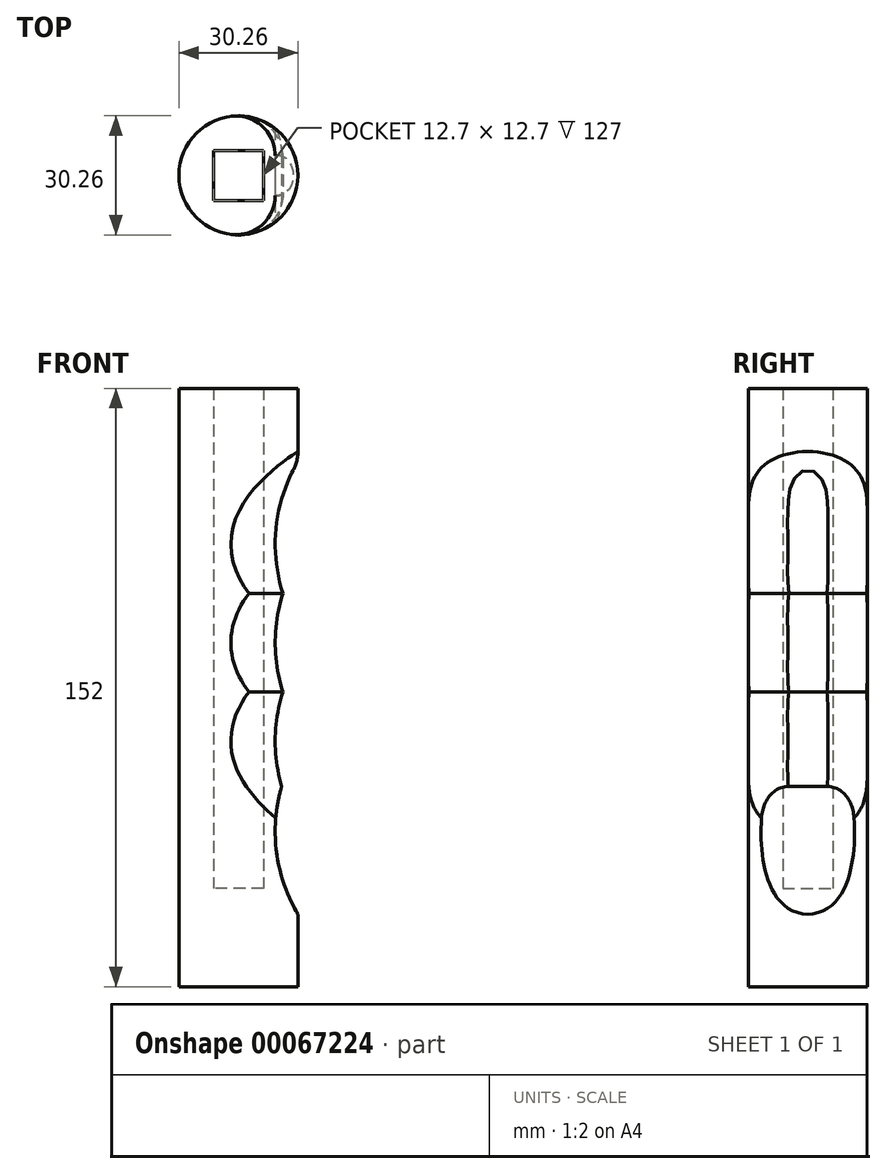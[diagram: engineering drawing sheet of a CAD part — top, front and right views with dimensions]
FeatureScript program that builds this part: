
annotation { "Feature Type Name" : "Feature", "Feature Type Description" : "" }
export const myFeature = defineFeature(function(context is Context, id is Id, definition is map)
    precondition{}
    {
        {
            var Q0;
            Q0=qCreatedBy(makeId("Top.planeOp"),FACE);
            var sketch = newSketch(context, id + "F0", { "sketchPlane" : qUnion([Q0])});
            skCircle(sketch, "E0", {"center": v(0, 0) * mm, "radius": 15.12 * mm});
            skLineSegment(sketch, "E1", {"start": v(-6.35, 0) * mm, "end": v(-6.35, -6.35) * mm});
            skLineSegment(sketch, "E2", {"start": v(-6.35, -6.35) * mm, "end": v(6.35, -6.35) * mm});
            skLineSegment(sketch, "E3", {"start": v(6.35, -6.35) * mm, "end": v(6.35, 6.35) * mm});
            skLineSegment(sketch, "E4", {"start": v(6.35, 6.35) * mm, "end": v(-6.35, 6.35) * mm});
            skLineSegment(sketch, "E5", {"start": v(-6.35, 0) * mm, "end": v(-6.35, 6.35) * mm});
            skSolve(sketch);
        }
        {
            var Q0;
            Q0=makeQuery(id+"F0.imprint","IMPRINT",FACE,{"disambiguationData":[TD([[makeQuery(id+"F0.imprint","IMPRINT",EDGE,{"derivedFrom":sQuery(id+"F0.wireOp",EDGE,"E0")}),1.0]])]});
            extrude(context, id + "F1", {"entities" : qUnion([Q0]), "depth" : 127 * mm});
        }
        {
            var Q0;
            Q0=makeQuery(id+"F1.opExtrude","CAP_FACE",FACE,{"disambiguationData":[OSD([sQuery(id+"F0.wireOp",EDGE,"E0"),sQuery(id+"F0.wireOp",EDGE,"268feebe-71f6-42c3-a029-8ffc5a6c32c5")])],"isStart":true});
            var sketch = newSketch(context, id + "F2", { "sketchPlane" : qUnion([Q0])});
            skCircle(sketch, "E6.0", {"center": v(0, 0) * mm, "radius": 15.12 * mm});
            skSolve(sketch);
        }
        {
            var Q0;
            Q0=makeQuery(id+"F2.imprint","IMPRINT",FACE,{"disambiguationData":[TD([[makeQuery(id+"F2.imprint","IMPRINT",EDGE,{"derivedFrom":sQuery(id+"F2.wireOp",EDGE,"E6.0")}),-1.0]])]});
            extrude(context, id + "F3", {"entities" : qUnion([Q0]), "operationType" : NewBodyOperationType.ADD, "depth" : 25 * mm});
        }
        {
            var Q0;
            Q0=qCreatedBy(makeId("Top.planeOp"),FACE);
            var sketch = newSketch(context, id + "F4", { "sketchPlane" : qUnion([Q0])});
            skLineSegment(sketch, "E7.0.1", {"start": v(-6.35, -6.35) * mm, "end": v(-6.35, 6.35) * mm});
            skLineSegment(sketch, "E7.0.3", {"start": v(-6.35, 6.35) * mm, "end": v(-6.35, -6.35) * mm});
            skLineSegment(sketch, "E8.0", {"start": v(-6.35, -6.35) * mm, "end": v(6.35, -6.35) * mm});
            skLineSegment(sketch, "E9.0", {"start": v(6.35, -6.35) * mm, "end": v(6.35, 6.35) * mm});
            skLineSegment(sketch, "E10.0", {"start": v(6.35, 6.35) * mm, "end": v(-6.35, 6.35) * mm});
            skSolve(sketch);
        }
        {
            var Q0;
            Q0=qCreatedBy(makeId("Front.planeOp"),FACE);
            var sketch = newSketch(context, id + "F5", { "sketchPlane" : qUnion([Q0])});
            skLineSegment(sketch, "E11", {"start": v(15.12, 127) * mm, "end": v(15.12, -25) * mm});
            skLineSegment(sketch, "E12", {"start": v(15.12, 127) * mm, "end": v(50.35, 127) * mm});
            skLineSegment(sketch, "E13", {"start": v(50.35, 127) * mm, "end": v(50.35, -25) * mm});
            skLineSegment(sketch, "E14", {"start": v(15.12, -25) * mm, "end": v(50.35, -25) * mm});
            skCircle(sketch, "E15", {"center": v(50.35, 14.4) * mm, "radius": 41 * mm});
            skCircle(sketch, "E16", {"center": v(50.35, 37.4) * mm, "radius": 41 * mm});
            skCircle(sketch, "E17", {"center": v(50.35, 62.4) * mm, "radius": 41 * mm});
            skCircle(sketch, "E18", {"center": v(50.35, 87.4) * mm, "radius": 41 * mm});
            skLineSegment(sketch, "E19", {"start": v(-6.88, 0) * mm, "end": v(-6.88, 127) * mm});
            skLineSegment(sketch, "E20", {"start": v(6.88, 127) * mm, "end": v(6.88, 0) * mm});
            skLineSegment(sketch, "E21", {"start": v(-15.12, -25) * mm, "end": v(-15.12, 127) * mm});
            skSolve(sketch);
        }
        {
            var Q0;
            Q0=qSketchRegion(id+"F5",true);
            extrude(context, id + "F6", {"entities" : qUnion([Q0]), "operationType" : NewBodyOperationType.REMOVE, "oppositeDirection" : true, "depth" : 50 * mm, "symmetric" : true});
        }
        {
            var Q0;
            {var subQ0=sQuery(id+"F5.wireOp",EDGE,"E18");Q0=makeQuery(id+"F6.boolean.opBoolean","INTERSECT",EDGE,{"derivedFrom":[makeQuery(id+"F3.boolean.opBoolean","MERGE",FACE,{"derivedFrom":[makeQuery(id+"F1.opExtrude","SWEPT_FACE",FACE,{"disambiguationData":[OSD([sQuery(id+"F0.wireOp",EDGE,"E0")])]}),makeQuery(id+"F3.opExtrude","SWEPT_FACE",FACE,{"disambiguationData":[OSD([sQuery(id+"F2.wireOp",EDGE,"E6.0")])]})]}),makeQuery(id+"F6.opExtrude","SWEPT_FACE",FACE,{"disambiguationData":[OSD([subQ0]),TDD([makeQuery(id+"F5.imprint","IMPRINT",EDGE,{"disambiguationData":[TD([[makeQuery(id+"F5.imprint","INTERSECT",VERTEX,{"disambiguationData":[OD(0.0)],"derivedFrom":[sQuery(id+"F5.wireOp",EDGE,"E11"),subQ0]}),-1.0]])],"derivedFrom":subQ0})])]})]});}
            var Q1;
            {var subQ0=sQuery(id+"F5.wireOp",EDGE,"E17");Q1=makeQuery(id+"F6.boolean.opBoolean","INTERSECT",EDGE,{"disambiguationData":[OD(0.0)],"derivedFrom":[makeQuery(id+"F3.boolean.opBoolean","MERGE",FACE,{"derivedFrom":[makeQuery(id+"F1.opExtrude","SWEPT_FACE",FACE,{"disambiguationData":[OSD([sQuery(id+"F0.wireOp",EDGE,"E0")])]}),makeQuery(id+"F3.opExtrude","SWEPT_FACE",FACE,{"disambiguationData":[OSD([sQuery(id+"F2.wireOp",EDGE,"E6.0")])]})]}),makeQuery(id+"F6.opExtrude","SWEPT_FACE",FACE,{"disambiguationData":[OSD([subQ0]),TDD([makeQuery(id+"F5.imprint","IMPRINT",EDGE,{"disambiguationData":[TD([[makeQuery(id+"F5.imprint","INTERSECT",VERTEX,{"disambiguationData":[OD(1.0)],"derivedFrom":[sQuery(id+"F5.wireOp",EDGE,"E16"),subQ0]}),1.0]])],"derivedFrom":subQ0})])]})]});}
            var Q2;
            {var subQ0=sQuery(id+"F5.wireOp",EDGE,"E17");Q2=makeQuery(id+"F6.boolean.opBoolean","INTERSECT",EDGE,{"disambiguationData":[OD(1.0)],"derivedFrom":[makeQuery(id+"F3.boolean.opBoolean","MERGE",FACE,{"derivedFrom":[makeQuery(id+"F1.opExtrude","SWEPT_FACE",FACE,{"disambiguationData":[OSD([sQuery(id+"F0.wireOp",EDGE,"E0")])]}),makeQuery(id+"F3.opExtrude","SWEPT_FACE",FACE,{"disambiguationData":[OSD([sQuery(id+"F2.wireOp",EDGE,"E6.0")])]})]}),makeQuery(id+"F6.opExtrude","SWEPT_FACE",FACE,{"disambiguationData":[OSD([subQ0]),TDD([makeQuery(id+"F5.imprint","IMPRINT",EDGE,{"disambiguationData":[TD([[makeQuery(id+"F5.imprint","INTERSECT",VERTEX,{"disambiguationData":[OD(1.0)],"derivedFrom":[sQuery(id+"F5.wireOp",EDGE,"E16"),subQ0]}),1.0]])],"derivedFrom":subQ0})])]})]});}
            var Q3;
            {var subQ0=sQuery(id+"F5.wireOp",EDGE,"E16");Q3=makeQuery(id+"F6.boolean.opBoolean","INTERSECT",EDGE,{"disambiguationData":[OD(1.0)],"derivedFrom":[makeQuery(id+"F3.boolean.opBoolean","MERGE",FACE,{"derivedFrom":[makeQuery(id+"F1.opExtrude","SWEPT_FACE",FACE,{"disambiguationData":[OSD([sQuery(id+"F0.wireOp",EDGE,"E0")])]}),makeQuery(id+"F3.opExtrude","SWEPT_FACE",FACE,{"disambiguationData":[OSD([sQuery(id+"F2.wireOp",EDGE,"E6.0")])]})]}),makeQuery(id+"F6.opExtrude","SWEPT_FACE",FACE,{"disambiguationData":[OSD([subQ0]),TDD([makeQuery(id+"F5.imprint","IMPRINT",EDGE,{"disambiguationData":[TD([[makeQuery(id+"F5.imprint","INTERSECT",VERTEX,{"disambiguationData":[OD(1.0)],"derivedFrom":[sQuery(id+"F5.wireOp",EDGE,"E15"),subQ0]}),1.0]])],"derivedFrom":subQ0})])]})]});}
            var Q4;
            {var subQ0=sQuery(id+"F5.wireOp",EDGE,"E15");Q4=makeQuery(id+"F6.boolean.opBoolean","INTERSECT",EDGE,{"derivedFrom":[makeQuery(id+"F3.boolean.opBoolean","MERGE",FACE,{"derivedFrom":[makeQuery(id+"F1.opExtrude","SWEPT_FACE",FACE,{"disambiguationData":[OSD([sQuery(id+"F0.wireOp",EDGE,"E0")])]}),makeQuery(id+"F3.opExtrude","SWEPT_FACE",FACE,{"disambiguationData":[OSD([sQuery(id+"F2.wireOp",EDGE,"E6.0")])]})]}),makeQuery(id+"F6.opExtrude","SWEPT_FACE",FACE,{"disambiguationData":[OSD([subQ0]),TDD([makeQuery(id+"F5.imprint","IMPRINT",EDGE,{"disambiguationData":[TD([[makeQuery(id+"F5.imprint","INTERSECT",VERTEX,{"disambiguationData":[OD(0.0)],"derivedFrom":[sQuery(id+"F5.wireOp",EDGE,"E11"),subQ0]}),1.0]])],"derivedFrom":subQ0})])]})]});}
            var Q5;
            {var subQ0=sQuery(id+"F5.wireOp",EDGE,"E16");Q5=makeQuery(id+"F6.boolean.opBoolean","INTERSECT",EDGE,{"disambiguationData":[OD(0.0)],"derivedFrom":[makeQuery(id+"F3.boolean.opBoolean","MERGE",FACE,{"derivedFrom":[makeQuery(id+"F1.opExtrude","SWEPT_FACE",FACE,{"disambiguationData":[OSD([sQuery(id+"F0.wireOp",EDGE,"E0")])]}),makeQuery(id+"F3.opExtrude","SWEPT_FACE",FACE,{"disambiguationData":[OSD([sQuery(id+"F2.wireOp",EDGE,"E6.0")])]})]}),makeQuery(id+"F6.opExtrude","SWEPT_FACE",FACE,{"disambiguationData":[OSD([subQ0]),TDD([makeQuery(id+"F5.imprint","IMPRINT",EDGE,{"disambiguationData":[TD([[makeQuery(id+"F5.imprint","INTERSECT",VERTEX,{"disambiguationData":[OD(1.0)],"derivedFrom":[sQuery(id+"F5.wireOp",EDGE,"E15"),subQ0]}),1.0]])],"derivedFrom":subQ0})])]})]});}
            fillet(context, id + "F7", {"entities" : qUnion([Q0, Q1, Q2, Q3, Q4, Q5]), "radius" : 10 * mm, "tangentPropagation" : true, "allowEdgeOverflow" : false});
        }
        {
            var Q0;
            Q0=qSketchRegion(id+"F4",true);
            var Q1;
            Q1=makeQuery(id+"F3.opExtrude","CAP_FACE",FACE,{"disambiguationData":[OSD([sQuery(id+"F0.wireOp",EDGE,"E1"),sQuery(id+"F0.wireOp",EDGE,"E2"),sQuery(id+"F0.wireOp",EDGE,"E3"),sQuery(id+"F0.wireOp",EDGE,"E4"),sQuery(id+"F0.wireOp",EDGE,"E5"),sQuery(id+"F2.wireOp",EDGE,"E6.0")])],"isStart":false});
            extrude(context, id + "F8", {"entities" : qUnion([Q0]), "operationType" : NewBodyOperationType.ADD, "endBound" : BoundingType.UP_TO_SURFACE, "oppositeDirection" : true, "endBoundEntityFace" : qUnion([Q1]), "depth" : 25 * mm});
        }
    });
